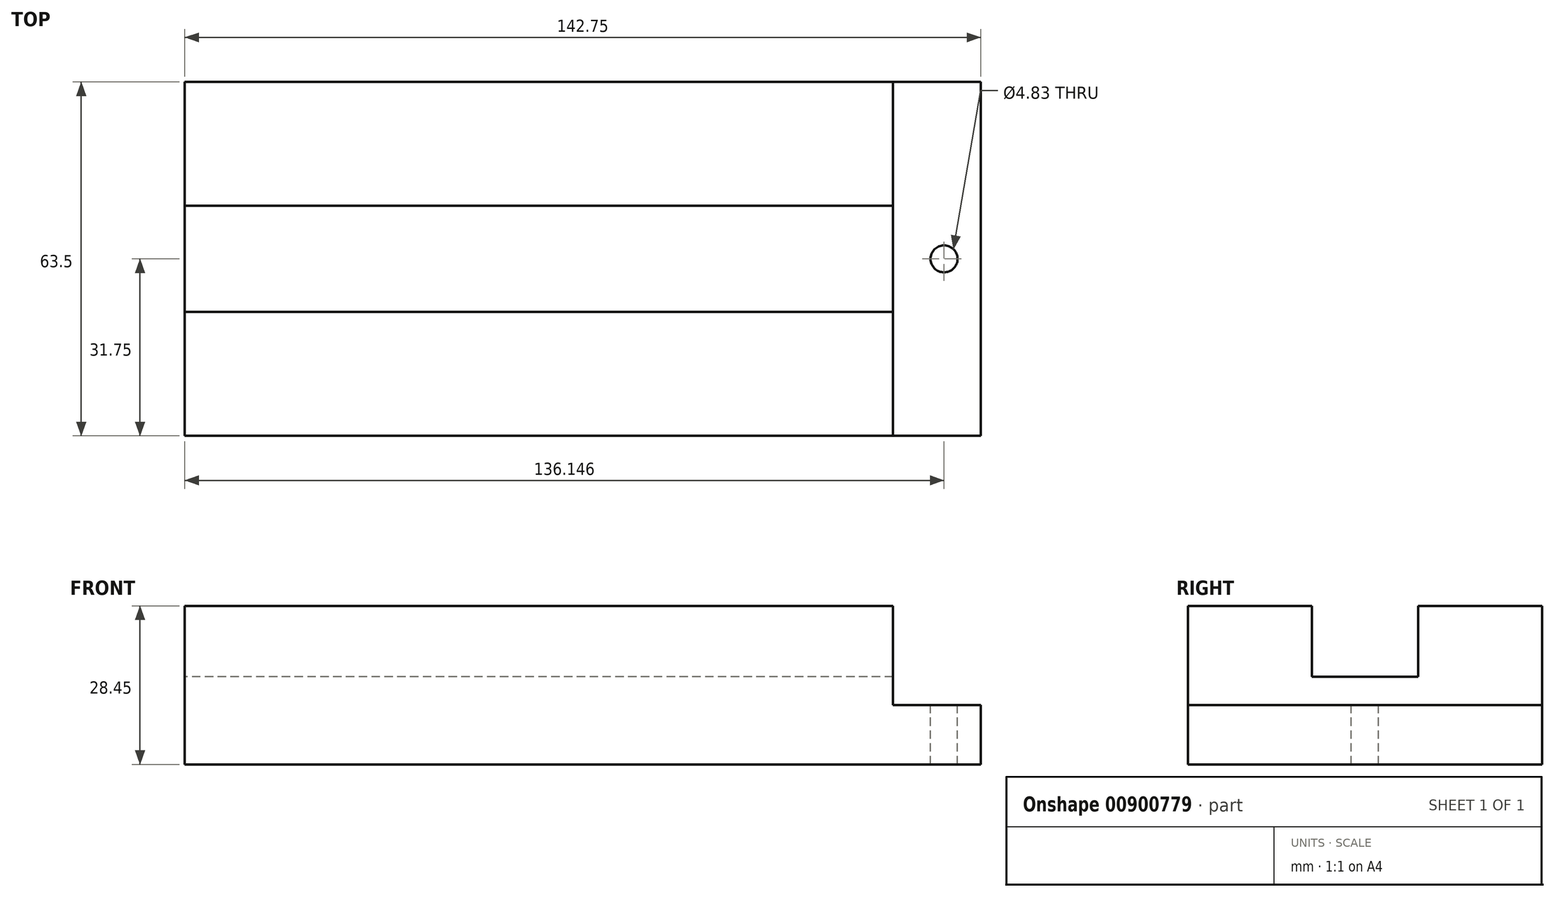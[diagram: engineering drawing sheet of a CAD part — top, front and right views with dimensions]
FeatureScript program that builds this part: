
annotation { "Feature Type Name" : "Feature", "Feature Type Description" : "" }
export const myFeature = defineFeature(function(context is Context, id is Id, definition is map)
    precondition{}
    {
        {
            var Q0;
            Q0=qCreatedBy(makeId("Front.planeOp"),FACE);
            var sketch = newSketch(context, id + "F0", { "sketchPlane" : qUnion([Q0])});
            skLineSegment(sketch, "E0.bottom", {"start": v(-142.75, 28.45) * mm, "end": v(-15.75, 28.45) * mm});
            skLineSegment(sketch, "E0.top", {"start": v(-142.75, 0) * mm, "end": v(0, 0) * mm});
            skLineSegment(sketch, "E0.left", {"start": v(-142.75, 28.45) * mm, "end": v(-142.75, 0) * mm});
            skLineSegment(sketch, "E0.right", {"start": v(0, 10.67) * mm, "end": v(0, 0) * mm});
            skLineSegment(sketch, "E1", {"start": v(-15.75, 28.45) * mm, "end": v(-15.75, 10.67) * mm});
            skLineSegment(sketch, "E2", {"start": v(-15.75, 10.67) * mm, "end": v(0, 10.67) * mm});
            skSolve(sketch);
        }
        {
            var Q0;
            Q0=makeQuery(id+"F0.imprint","IMPRINT",FACE,{"disambiguationData":[TD([[makeQuery(id+"F0.imprint","IMPRINT",EDGE,{"derivedFrom":sQuery(id+"F0.wireOp",EDGE,"E0.bottom")}),-1.0]])]});
            extrude(context, id + "F1", {"entities" : qUnion([Q0]), "depth" : 63.5 * mm, "offsetDistance" : 25.4 * mm});
        }
        {
            var Q0;
            Q0=makeQuery(id+"F1.opExtrude","SWEPT_FACE",FACE,{"disambiguationData":[OSD([sQuery(id+"F0.wireOp",EDGE,"E2")])]});
            var sketch = newSketch(context, id + "F2", { "sketchPlane" : qUnion([Q0])});
            skCircle(sketch, "E3", {"center": v(-6.6, -31.75) * mm, "radius": 2.41 * mm});
            skSolve(sketch);
        }
        {
            var Q0;
            Q0=makeQuery(id+"F2.imprint","IMPRINT",FACE,{"disambiguationData":[TD([[makeQuery(id+"F2.imprint","IMPRINT",EDGE,{"derivedFrom":sQuery(id+"F2.wireOp",EDGE,"E3")}),1.0]])]});
            extrude(context, id + "F3", {"entities" : qUnion([Q0]), "operationType" : NewBodyOperationType.REMOVE, "endBound" : BoundingType.THROUGH_ALL, "oppositeDirection" : true, "depth" : 25.4 * mm, "offsetDistance" : 25.4 * mm});
        }
        {
            var Q0;
            Q0=makeQuery(id+"F1.opExtrude","SWEPT_FACE",FACE,{"disambiguationData":[OSD([sQuery(id+"F0.wireOp",EDGE,"E0.left")])]});
            var sketch = newSketch(context, id + "F4", { "sketchPlane" : qUnion([Q0])});
            skLineSegment(sketch, "E4.bottom", {"start": v(22.23, 15.75) * mm, "end": v(41.27, 15.75) * mm});
            skLineSegment(sketch, "E4.top", {"start": v(22.22, 35.78) * mm, "end": v(41.27, 35.78) * mm});
            skLineSegment(sketch, "E4.left", {"start": v(22.23, 15.75) * mm, "end": v(22.23, 35.78) * mm});
            skLineSegment(sketch, "E4.right", {"start": v(41.27, 15.75) * mm, "end": v(41.27, 35.78) * mm});
            skSolve(sketch);
        }
        {
            var Q0;
            {var subQ0=sQuery(id+"F4.wireOp",EDGE,"E4.bottom");Q0=makeQuery(id+"F4.imprint","IMPRINT",FACE,{"disambiguationData":[TD([[makeQuery(id+"F4.imprint","IMPRINT",EDGE,{"derivedFrom":subQ0}),1.0]])]});}
            extrude(context, id + "F5", {"entities" : qUnion([Q0]), "operationType" : NewBodyOperationType.REMOVE, "endBound" : BoundingType.THROUGH_ALL, "oppositeDirection" : true, "depth" : 25.4 * mm, "offsetDistance" : 25.4 * mm});
        }
    });
